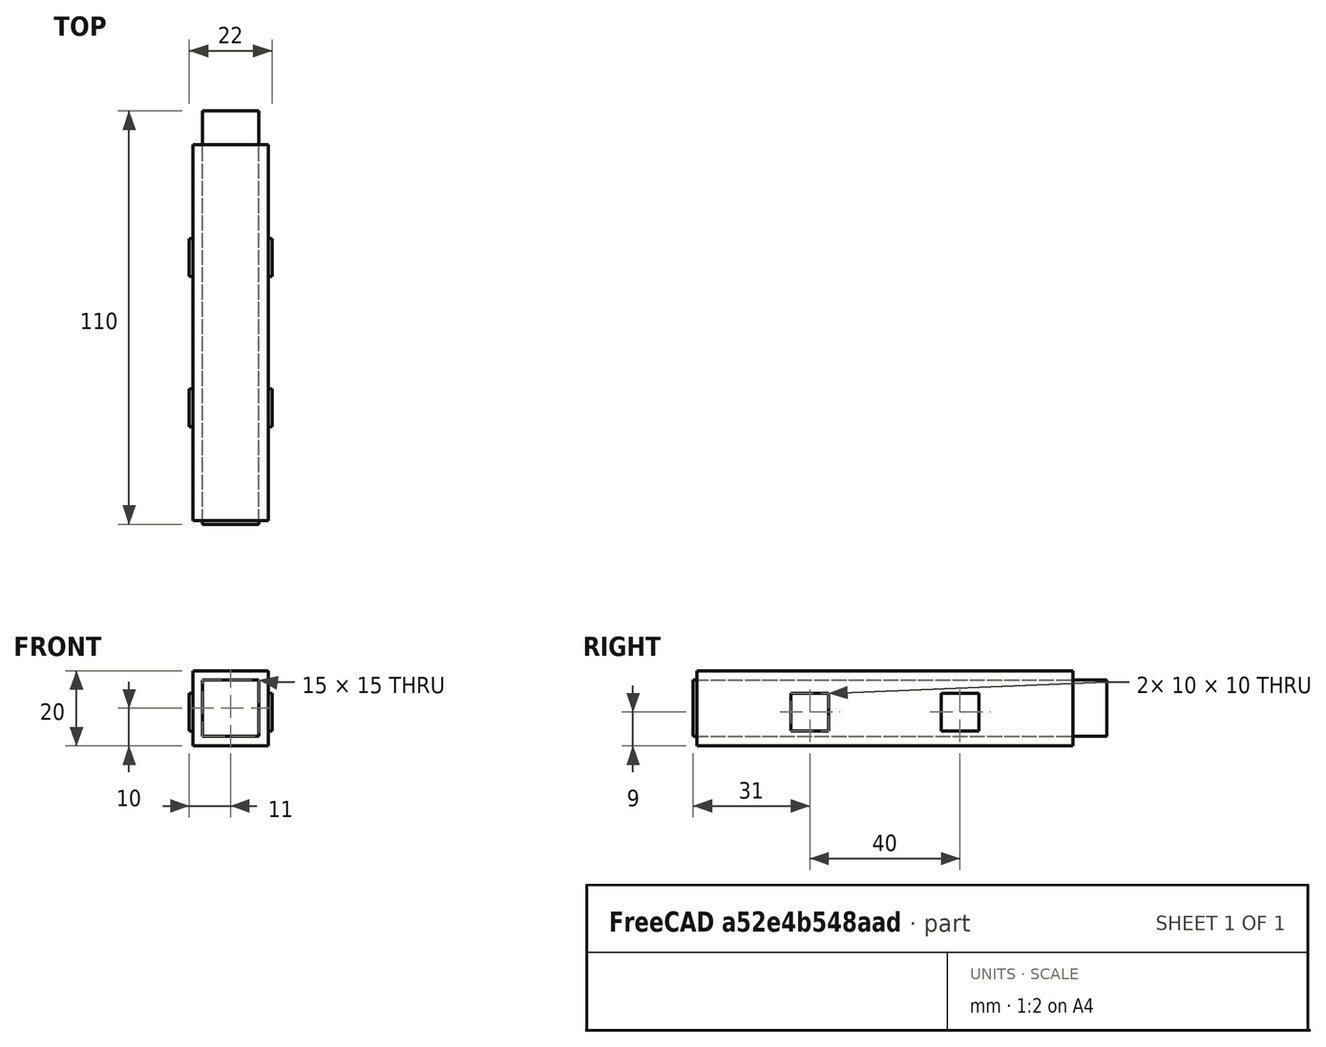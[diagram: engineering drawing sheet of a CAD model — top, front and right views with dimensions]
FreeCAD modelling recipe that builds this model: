
FCSTD DOCUMENT  (FreeCAD 0.21R33675 (Git))
Label: ThermalSim1
License: All rights reserved
LicenseURL: http://en.wikipedia.org/wiki/All_rights_reserved
objects: Part::Box×7, Fem::ConstraintHeatflux×3, Fem::FemSolverObjectPython×2, App::MaterialObjectPython×2, Part::Cut×1, Fem::ConstraintInitialTemperature×1, Part::MultiFuse×1, Fem::FemMeshShapeNetgenObject×1, Fem::FemAnalysis×1
note: 9 computed .brp shape members not serialized (recipe doc carries the construction recipe); baked Part::Feature solids carry a one-line shape summary decoded from their .brp

FEATURE [Part::Box] Box  label="Cube"
  AttacherType = Attacher::AttachEngine3D
  Height = 20
  Length = 20
  Width = 100
FEATURE [Part::Box] Box001  label="Cube001"
  AttacherType = Attacher::AttachEngine3D
  Height = 15
  Length = 15
  Placement = pos=(2.5,-1,2.5) rot=(0,0,1;0rad)
  Width = 110
FEATURE [Part::Cut] Cut
  Base = -> Box
  Tool = -> Box001
FEATURE [Part::Box] Box002  label="Cube002"
  AttacherType = Attacher::AttachEngine3D
  Height = 10
  Length = 1
  Placement = pos=(20,25,4) rot=(0,0,1;0rad)
  Width = 10
FEATURE [Fem::ConstraintInitialTemperature] ConstraintInitialTemperature
  NormalDirection = (0,0,1)
  initialTemperature = 300
FEATURE [Fem::FemSolverObjectPython] SolverCcxTools  # FEM object (typed FeaturePython)
  AnalysisType = 2
  BeamShellResultOutput3D = false
  BucklingFactors = 1
  EigenmodeHighLimit = 1000000
  EigenmodeLowLimit = 0
  EigenmodesCount = 10
  GeometricalNonlinearity = 0
  IterationsControlParameterCutb = 0.25,0.5,0.75,0.85,,,1.5,
  IterationsControlParameterIter = 4,8,9,200,10,400,,200,,
  IterationsControlParameterTimeUse = false
  IterationsThermoMechMaximum = 200
  IterationsUserDefinedIncrementations = false
  IterationsUserDefinedTimeStepLength = false
  MaterialNonlinearity = 0
  MatrixSolverType = 0
  SplitInputWriter = false
  ThermoMechSteadyState = false
  TimeEnd = 120
  TimeInitialStep = 119
FEATURE [Part::Box] Box003  label="Cube003"
  AttacherType = Attacher::AttachEngine3D
  Height = 10
  Length = 1
  Placement = pos=(20,65,4) rot=(0,0,1;0rad)
  Width = 10
FEATURE [Part::Box] Box004  label="Cube004"
  AttacherType = Attacher::AttachEngine3D
  Height = 10
  Length = 1
  Placement = pos=(-1,65,4) rot=(0,0,1;0rad)
  Width = 10
FEATURE [Part::Box] Box005  label="Cube005"
  AttacherType = Attacher::AttachEngine3D
  Height = 10
  Length = 1
  Placement = pos=(-1,25,4) rot=(0,0,1;0rad)
  Width = 10
FEATURE [Part::MultiFuse] Fusion
  Shapes = -> [Cut,Box002,Box003,Box004,Box005]
FEATURE [App::MaterialObjectPython] MaterialSolid  # material (typed FeaturePython)
  Category = 0
  Material = AuthorAndLicense=Uwe Stöhr,CardName=Aluminum-Generic,Density=2700 kg/m^3,ElectricalConductivity=370370.4 S/m,Father=Metal,KindOfMaterial=Aluminium,+9 more (map truncated)
  References = -> [Fusion]
FEATURE [Fem::ConstraintHeatflux] ConstraintHeatflux  label="MOSFET1"
  AmbientTemp = 300
  ConstraintType = 0
  DFlux = 250000
  FilmCoef = 1
  NormalDirection = (-1,0,0)
  Normals = (36) [(-1,0,0),(-1,0,0),(-1,0,0),(-1,0,0),(-1,0,0),(-1,0,0),(-1,0,0),(-1,0,0),(-1,0,0),(-1,0,0),(-1,0,0),(-1,0,0),(-1,0,0),(-1,0,0),(-1,0,0),(-1,0,0),+20 more]
  Points = (36) [(-1,75,4),(-1,75,9),(-1,75,14),(-1,70,4),(-1,70,9),(-1,70,14),(-1,65,4),(-1,65,9),(-1,65,14),(-1,35,4),(-1,35,9),(-1,35,14),(-1,30,4),(-1,30,9),+22 more]
  References = -> [Fusion]
FEATURE [Fem::ConstraintHeatflux] ConstraintHeatflux001  label="Convectie"
  AmbientTemp = 300
  ConstraintType = 1
  DFlux = 0
  FilmCoef = 10
  NormalDirection = (0,0,1)
  Normals = (108) [(0,0,1),(0,0,1),(0,0,1),(0,0,1),(0,0,1),(0,0,1),(0,0,1),(0,0,1),(0,0,1),(0,0,1),(0,0,1),(0,0,1),(1,0,0),(1,0,0),(1,0,0),(1,0,0),(1,0,0),(1,0,0),+90 more]
  Points = (108) [(0,0,20),(10,0,20),(20,0,20),(0,33.3333,20),(10,33.3333,20),(20,33.3333,20),(0,66.6667,20),(10,66.6667,20),(20,66.6667,20),(0,100,20),(10,100,20),+97 more]
  References = -> [Fusion]
FEATURE [Fem::FemMeshShapeNetgenObject] FEMMeshNetgen
  Fineness = 2
  GrowthRate = 0.3
  MaxSize = 1000
  NbSegsPerEdge = 1
  NbSegsPerRadius = 2
  Optimize = true
  SecondOrder = true
  Shape = -> Fusion
FEATURE [Part::Box] Box006  label="Cube006"
  AttacherType = Attacher::AttachEngine3D
  Height = 15
  Length = 15
  Placement = pos=(2.5,-1,2.5) rot=(0,0,1;0rad)
  Width = 110
FEATURE [App::MaterialObjectPython] MaterialFluid  # material (typed FeaturePython)
  Category = 1
  Material = CardName=Air,Density=1.204 kg/m^3,Description=Dry air properties at 20 Degrees Celsius and 1 atm,DynamicViscosity=1.80e-5 kg/m/s,+11 more (map truncated)
  References = -> [Box006]
FEATURE [Fem::ConstraintHeatflux] ConstraintHeatflux002
  AmbientTemp = 300
  ConstraintType = 1
  DFlux = 0
  FilmCoef = 10
  NormalDirection = (0,-1,0)
  Normals = (9) [(0,-1,0),(0,-1,0),(0,-1,0),(0,-1,0),(0,-1,0),(0,-1,0),(0,-1,0),(0,-1,0),(0,-1,0)]
  Points = (9) [(2.5,-1,2.5),(2.5,-1,10),(2.5,-1,17.5),(10,-1,2.5),(10,-1,10),(10,-1,17.5),(17.5,-1,2.5),(17.5,-1,10),(17.5,-1,17.5)]
  References = -> [Box006]
FEATURE [Fem::FemSolverObjectPython] SolverElmer  # FEM object (typed FeaturePython)
  BDFOrder = 2
  CoordinateSystem = 0
  OutputIntervals = [1]
  SimulationType = 1
  SteadyStateMaxIterations = 1
  SteadyStateMinIterations = 0
  TimestepIntervals = [100]
  TimestepSizes = [0.1]
FEATURE [Fem::FemAnalysis] Analysis
  Group = -> [MaterialSolid,ConstraintHeatflux,ConstraintInitialTemperature,ConstraintHeatflux001,SolverCcxTools,FEMMeshNetgen,MaterialFluid,ConstraintHeatflux002,SolverElmer]
